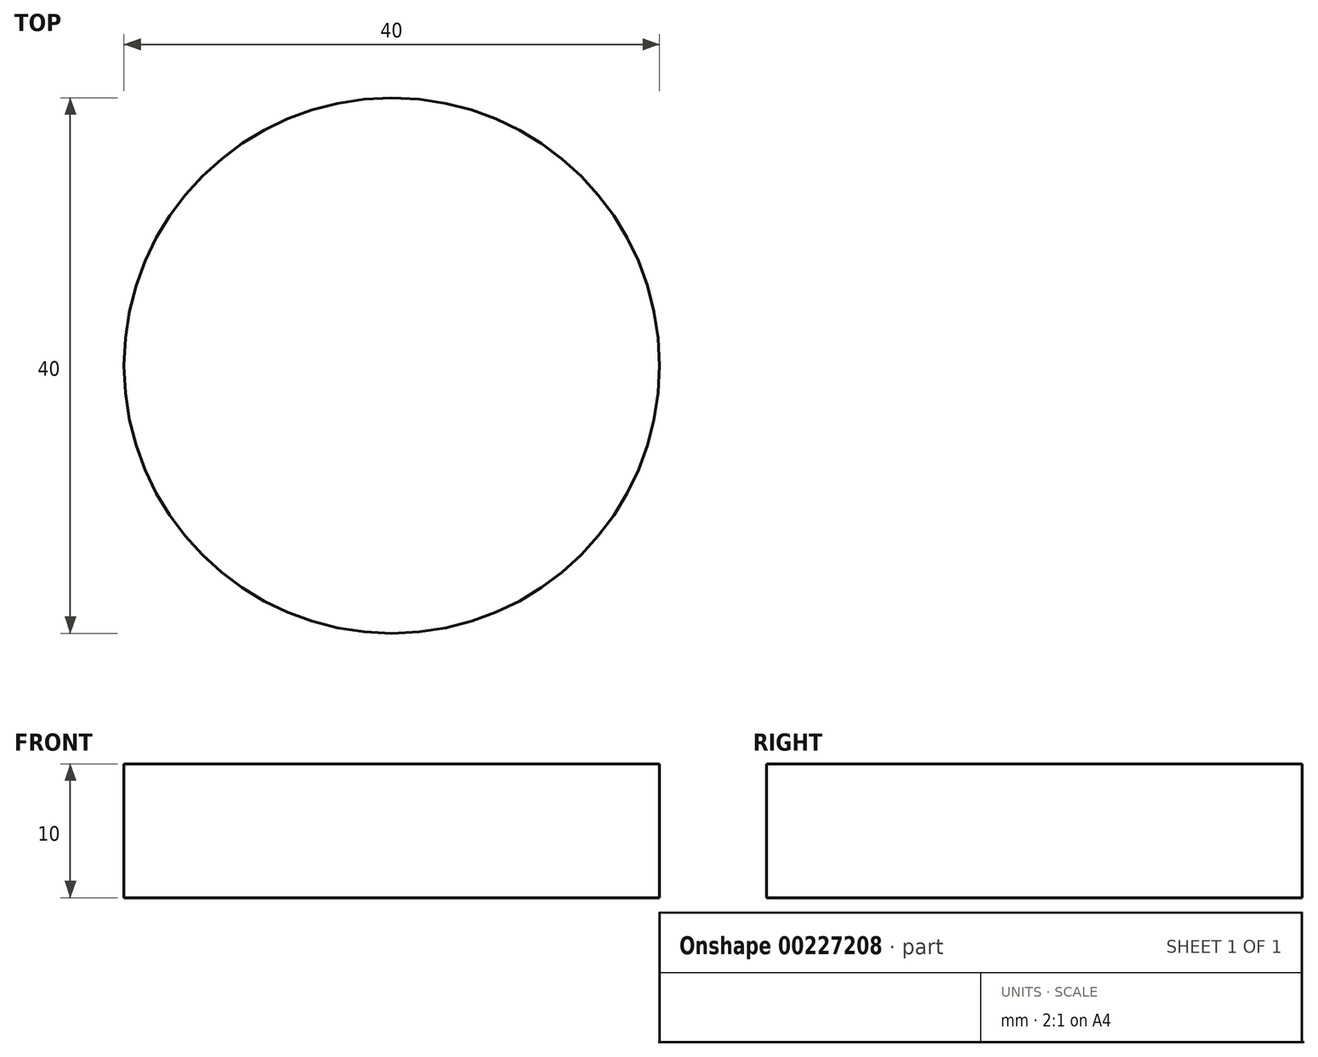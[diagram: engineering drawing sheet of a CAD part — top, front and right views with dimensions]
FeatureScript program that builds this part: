
annotation { "Feature Type Name" : "Feature", "Feature Type Description" : "" }
export const myFeature = defineFeature(function(context is Context, id is Id, definition is map)
    precondition{}
    {
        {
            var Q0;
            Q0=qCreatedBy(makeId("Top.planeOp"),FACE);
            var sketch = newSketch(context, id + "F0", { "sketchPlane" : qUnion([Q0])});
            skCircle(sketch, "E0", {"center": v(0, 0) * mm, "radius": 20 * mm});
            skSolve(sketch);
        }
        {
            var Q0;
            Q0 = qSketchRegion(id + "F0", true);
            extrude(context, id + "F1", {"entities" : qUnion([Q0]), "depth" : 10 * mm});
        }
    });
